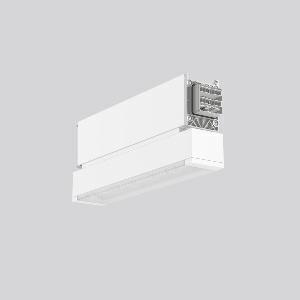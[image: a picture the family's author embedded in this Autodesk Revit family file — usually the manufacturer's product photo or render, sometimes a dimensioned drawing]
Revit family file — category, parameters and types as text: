
# Revit family: linedo_module_rq_9503rq_762_437_00c_fb33
name_source: partatom
category: Lighting Fixtures
units: mm (PartAtom-declared; Revit-internal decimal feet)

## family parameters
Cut with Voids When Loaded = No
Host = Face
Light Source = No
Part Type = Normal
Room Calculation Point = No
Round Connector Dimension = Use Diameter
Shared = No

## types (1)
- LINEDO Module RQ (1 x LED Modul 763, 450 lm, 6300)
    Apparent Load = 6 VA
    CIE Flux Codes = 39 72 97 99 100
    Color Rendering = 70
    Color Temperature = 6300
    Default Elevation = 1800 mm
    Description = LINEDO, 6 W, 450 lm, 763, white, on/off
Continuous line luminaire, L 342 B 58 H 131, SBS, 3 h, emergency-210 lm, DALI-Sibe
    Height = 131 mm
    Lamp = 1 x LED Modul 763
    Lamp Light Flux = 450 lm
    Lamp count = 1
    Length = 342 mm
    Lifetime = 50000 h
    Luminous efficacy = 75 lm/W
    Manufacturer = RZB
    ModVariant = No
    Model = 9503RQ.762.437.00C
    Mounting Place = Ceiling
    Mounting Type = Surface mounted
    Number of Poles = 1
    OnlyDefault = Yes
    Power Factor = 1
    Product Name = LINEDO Module RQ
    Product group = Surface mounted continuous line luminaire system
    ProductGroupID = 310
    Protection Class = Protection class I
    Protection Degree = IP 54
    RLX_Detail_Level = 1
    RLX_Emergency_Light_Flux = 210 lm
    RLX_Emergency_Type = 3
    RLX_Emergency_Type_DB = Yes
    RlxData = <blob elided: 31993 chars, md5=afc12185>
    Socket = socket
    Standby Power = 0 W
    System Light Flux = 450 lm
    System Power = 6 W
    Type Comments = Product without accessories
    Type Image = 9503rf.762.430.00c.jpg
    URL = http://relux.com
    VarID = ---
    Voltage = 230 V
    Voltage Range = 220-240 V
    Weight = 0.00 kg
    Width = 58 mm

## geometry (parser evidence)
native form markers: Blend x4, Sweep x11
no freeform markers — native parametric forms only
